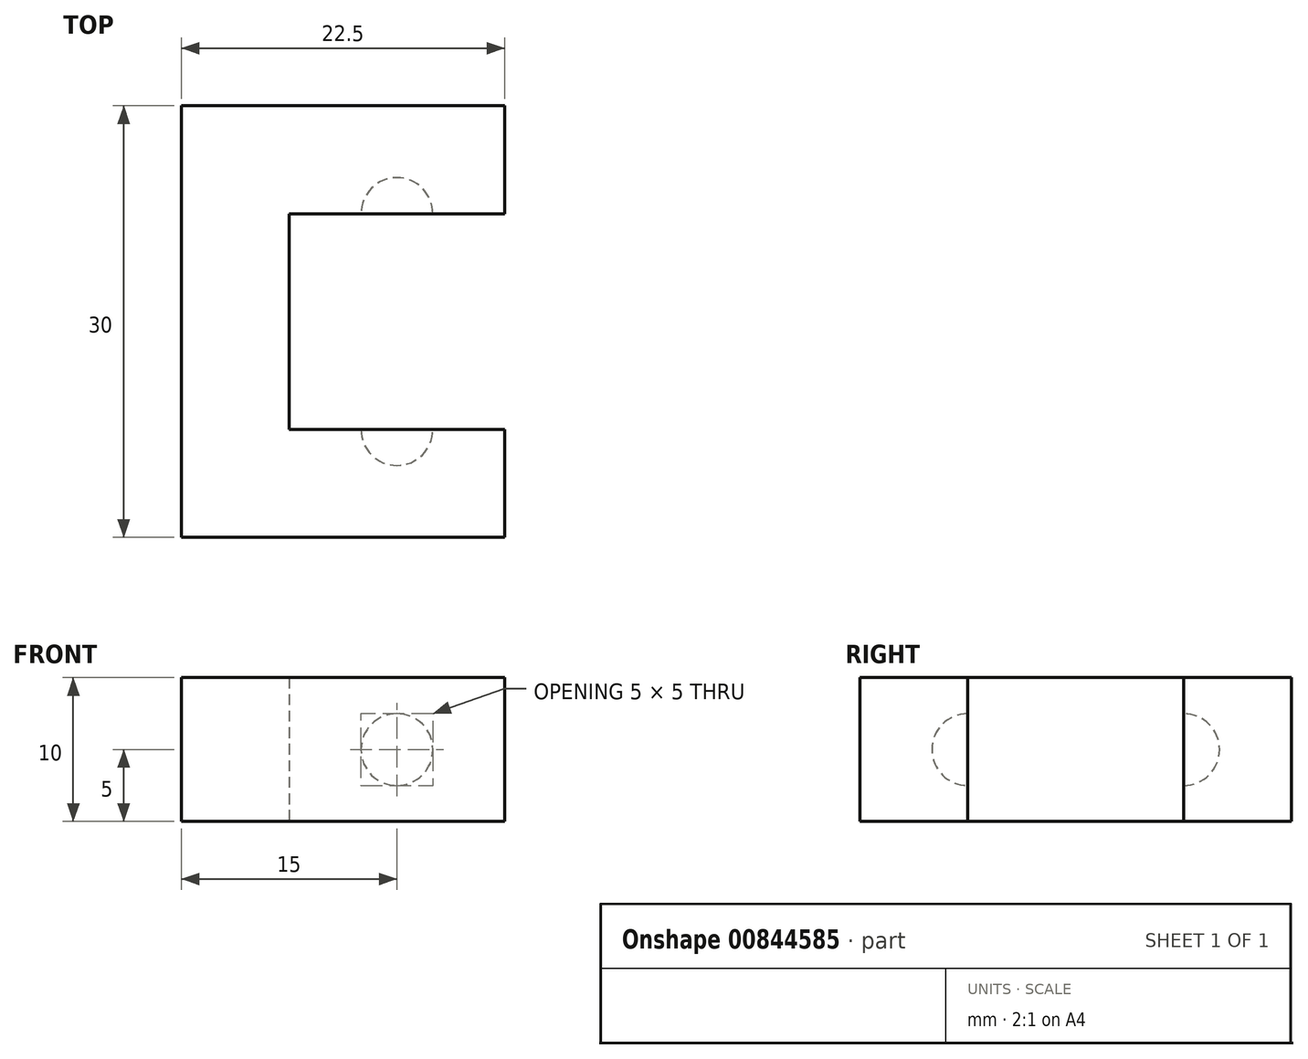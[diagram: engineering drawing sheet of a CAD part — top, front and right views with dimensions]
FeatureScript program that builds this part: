
annotation { "Feature Type Name" : "Feature", "Feature Type Description" : "" }
export const myFeature = defineFeature(function(context is Context, id is Id, definition is map)
    precondition{}
    {
        {
            var Q0;
            Q0=qCreatedBy(makeId("Top.planeOp"),FACE);
            var sketch = newSketch(context, id + "F0", { "sketchPlane" : qUnion([Q0])});
            skLineSegment(sketch, "E0.top", {"start": v(22.5, 15) * mm, "end": v(0, 15) * mm});
            skPoint(sketch, "E0.middle", {"position": v(0, 0) * mm});
            skPoint(sketch, "E1", {"position": v(22.5, 7.5) * mm});
            skLineSegment(sketch, "E2.bottom", {"start": v(7.5, 7.5) * mm, "end": v(22.5, 7.5) * mm});
            skLineSegment(sketch, "E2.left", {"start": v(7.5, 7.5) * mm, "end": v(7.5, 0) * mm});
            skLineSegment(sketch, "E3.trimOffspring", {"start": v(22.5, 7.5) * mm, "end": v(22.5, 15) * mm});
            skLineSegment(sketch, "E4", {"start": v(0, 0) * mm, "end": v(7.5, 0) * mm});
            skLineSegment(sketch, "E5", {"start": v(0, 15) * mm, "end": v(0, 0) * mm});
            skSolve(sketch);
        }
        {
            var Q0;
            Q0 = qSketchRegion(id + "F0", true);
            extrude(context, id + "F1", {"entities" : qUnion([Q0]), "depth" : 10 * mm, "offsetDistance" : 25 * mm});
        }
        {
            var Q0;
            Q0=makeQuery(id+"F1.opExtrude","SWEPT_FACE",FACE,{"disambiguationData":[OSD([sQuery(id+"F0.wireOp",EDGE,"E2.bottom")])]});
            var sketch = newSketch(context, id + "F2", { "sketchPlane" : qUnion([Q0])});
            skArc(sketch, "E6", {"start": v(15, 7.5) * mm, "mid": v(12.5, 5) * mm, "end": v(15, 2.5) * mm});
            skLineSegment(sketch, "E7", {"start": v(15, 7.5) * mm, "end": v(15, 2.5) * mm});
            skSolve(sketch);
        }
        {
            var Q0;
            Q0=makeQuery(id+"F2.imprint","IMPRINT",FACE,{"disambiguationData":[TD([[makeQuery(id+"F2.imprint","IMPRINT",EDGE,{"derivedFrom":sQuery(id+"F2.wireOp",EDGE,"E6")}),1.0]])]});
            var Q1;
            Q1=sQuery(id+"F2.wireOp",EDGE,"E7");
            revolve(context, id + "F3", {"operationType" : NewBodyOperationType.REMOVE, "surfaceOperationType" : NewSurfaceOperationType.NEW, "entities" : qUnion([Q0]), "axis" : qUnion([Q1]), "revolveType" : RevolveType.FULL, "oppositeDirection" : true});
        }
        {
            var Q0;
            Q0=makeQuery(id+"F1.opExtrude","SWEPT_BODY",BODY,{"disambiguationData":[OSD([sQuery(id+"F0.wireOp",EDGE,"E0.top"),sQuery(id+"F0.wireOp",EDGE,"E0.right"),sQuery(id+"F0.wireOp",EDGE,"E2.bottom"),sQuery(id+"F0.wireOp",EDGE,"E2.left"),sQuery(id+"F0.wireOp",EDGE,"E3.trimOffspring"),sQuery(id+"F0.wireOp",EDGE,"E4")])]});
            var Q1;
            Q1=qCreatedBy(makeId("Front.planeOp"),FACE);
            mirror(context, id + "F4", {"operationType" : NewBodyOperationType.ADD, "entities" : qUnion([Q0]), "mirrorPlane" : qUnion([Q1])});
        }
    });
